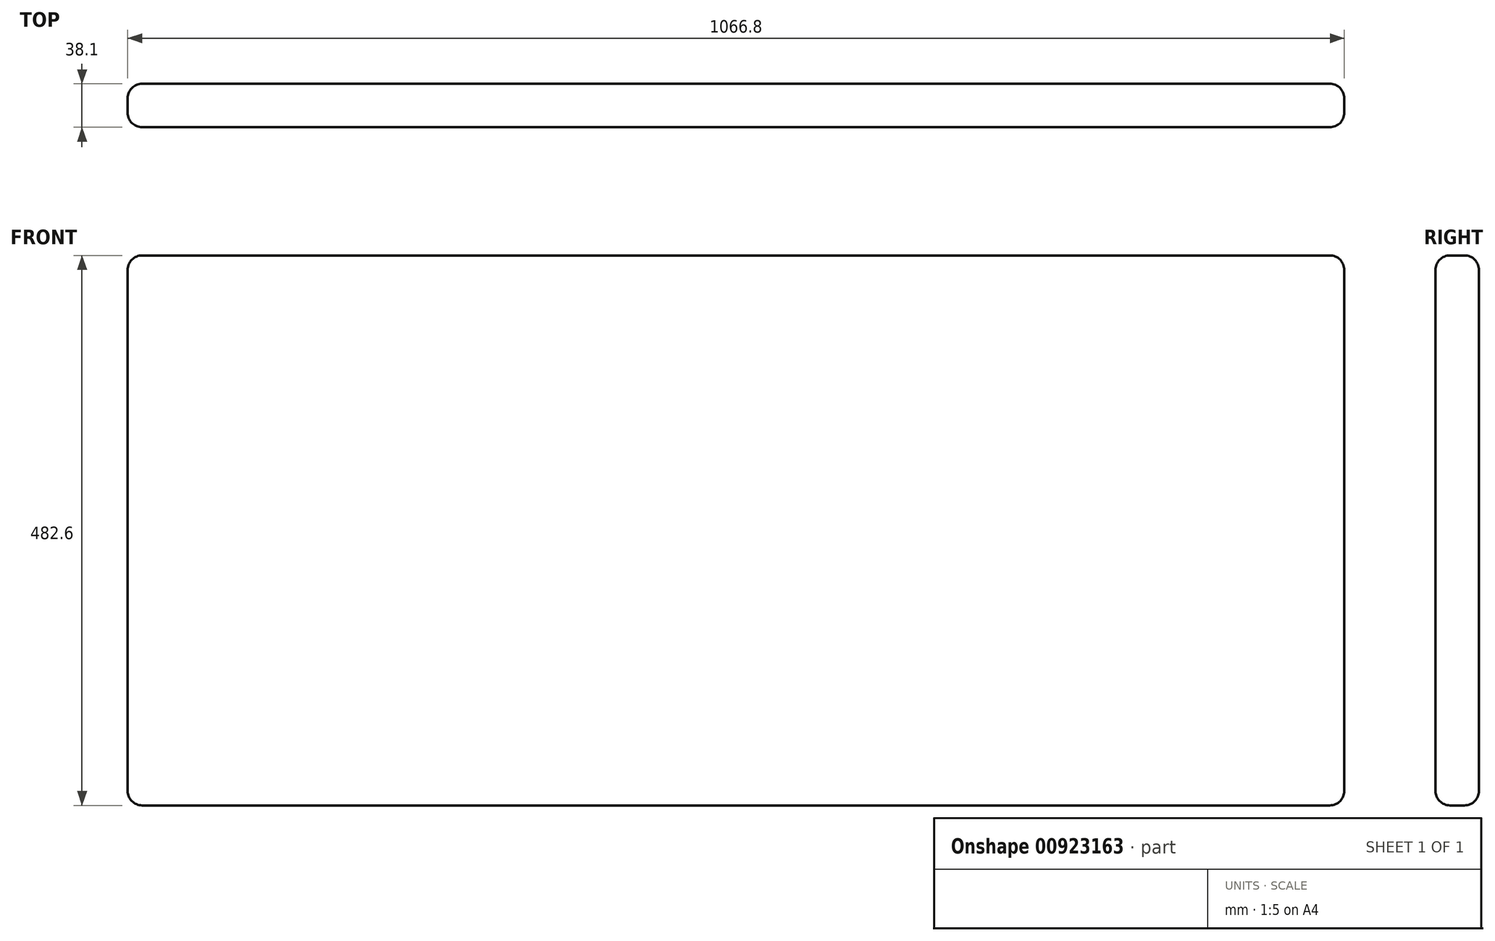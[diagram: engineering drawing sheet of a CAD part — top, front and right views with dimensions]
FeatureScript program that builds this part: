
annotation { "Feature Type Name" : "Feature", "Feature Type Description" : "" }
export const myFeature = defineFeature(function(context is Context, id is Id, definition is map)
    precondition{}
    {
        {
            var Q0;
            Q0=qCreatedBy(makeId("Front.planeOp"),FACE);
            var sketch = newSketch(context, id + "F0", { "sketchPlane" : qUnion([Q0])});
            skLineSegment(sketch, "E0.bottom", {"start": v(-533.4, 241.3) * mm, "end": v(533.4, 241.3) * mm});
            skLineSegment(sketch, "E0.top", {"start": v(-533.4, -241.3) * mm, "end": v(533.4, -241.3) * mm});
            skLineSegment(sketch, "E0.left", {"start": v(-533.4, 241.3) * mm, "end": v(-533.4, -241.3) * mm});
            skLineSegment(sketch, "E0.right", {"start": v(533.4, 241.3) * mm, "end": v(533.4, -241.3) * mm});
            skPoint(sketch, "E0.middle", {"position": v(0, 0) * mm});
            skSolve(sketch);
        }
        {
            var Q0;
            Q0=makeQuery(id+"F0.imprint","IMPRINT",FACE,{"disambiguationData":[TD([[makeQuery(id+"F0.imprint","IMPRINT",EDGE,{"derivedFrom":sQuery(id+"F0.wireOp",EDGE,"E0.bottom")}),-1.0]])]});
            extrude(context, id + "F1", {"entities" : qUnion([Q0]), "endBound" : BoundingType.SYMMETRIC, "depth" : 38.1 * mm, "offsetDistance" : 25.4 * mm});
        }
        {
            var Q0;
            Q0=makeQuery(id+"F1.opExtrude","CAP_EDGE",EDGE,{"disambiguationData":[OSD([sQuery(id+"F0.wireOp",EDGE,"E0.bottom")])],"isStart":true});
            var Q1;
            Q1=makeQuery(id+"F1.opExtrude","CAP_EDGE",EDGE,{"disambiguationData":[OSD([sQuery(id+"F0.wireOp",EDGE,"E0.bottom")])],"isStart":false});
            var Q2;
            Q2=makeQuery(id+"F1.opExtrude","CAP_EDGE",EDGE,{"disambiguationData":[OSD([sQuery(id+"F0.wireOp",EDGE,"E0.top")])],"isStart":true});
            var Q3;
            Q3=makeQuery(id+"F1.opExtrude","CAP_EDGE",EDGE,{"disambiguationData":[OSD([sQuery(id+"F0.wireOp",EDGE,"E0.right")])],"isStart":true});
            var Q4;
            Q4=makeQuery(id+"F1.opExtrude","CAP_EDGE",EDGE,{"disambiguationData":[OSD([sQuery(id+"F0.wireOp",EDGE,"E0.right")])],"isStart":false});
            var Q5;
            Q5=makeQuery(id+"F1.opExtrude","CAP_EDGE",EDGE,{"disambiguationData":[OSD([sQuery(id+"F0.wireOp",EDGE,"E0.top")])],"isStart":false});
            var Q6;
            Q6=makeQuery(id+"F1.opExtrude","CAP_EDGE",EDGE,{"disambiguationData":[OSD([sQuery(id+"F0.wireOp",EDGE,"E0.left")])],"isStart":false});
            var Q7;
            Q7=makeQuery(id+"F1.opExtrude","CAP_EDGE",EDGE,{"disambiguationData":[OSD([sQuery(id+"F0.wireOp",EDGE,"E0.left")])],"isStart":true});
            var Q8;
            Q8=makeQuery(id+"F1.opExtrude","SWEPT_EDGE",EDGE,{"disambiguationData":[OSD([sQuery(id+"F0.wireOp",EDGE,"E0.bottom"),sQuery(id+"F0.wireOp",EDGE,"E0.left")])]});
            var Q9;
            Q9=makeQuery(id+"F1.opExtrude","SWEPT_EDGE",EDGE,{"disambiguationData":[OSD([sQuery(id+"F0.wireOp",EDGE,"E0.bottom"),sQuery(id+"F0.wireOp",EDGE,"E0.right")])]});
            var Q10;
            Q10=makeQuery(id+"F1.opExtrude","SWEPT_EDGE",EDGE,{"disambiguationData":[OSD([sQuery(id+"F0.wireOp",EDGE,"E0.top"),sQuery(id+"F0.wireOp",EDGE,"E0.right")])]});
            var Q11;
            Q11=makeQuery(id+"F1.opExtrude","SWEPT_EDGE",EDGE,{"disambiguationData":[OSD([sQuery(id+"F0.wireOp",EDGE,"E0.top"),sQuery(id+"F0.wireOp",EDGE,"E0.left")])]});
            fillet(context, id + "F2", {"entities" : qUnion([Q0, Q1, Q2, Q3, Q4, Q5, Q6, Q7, Q8, Q9, Q10, Q11]), "radius" : 12.7 * mm, "tangentPropagation" : true, "allowEdgeOverflow" : false});
        }
    });
